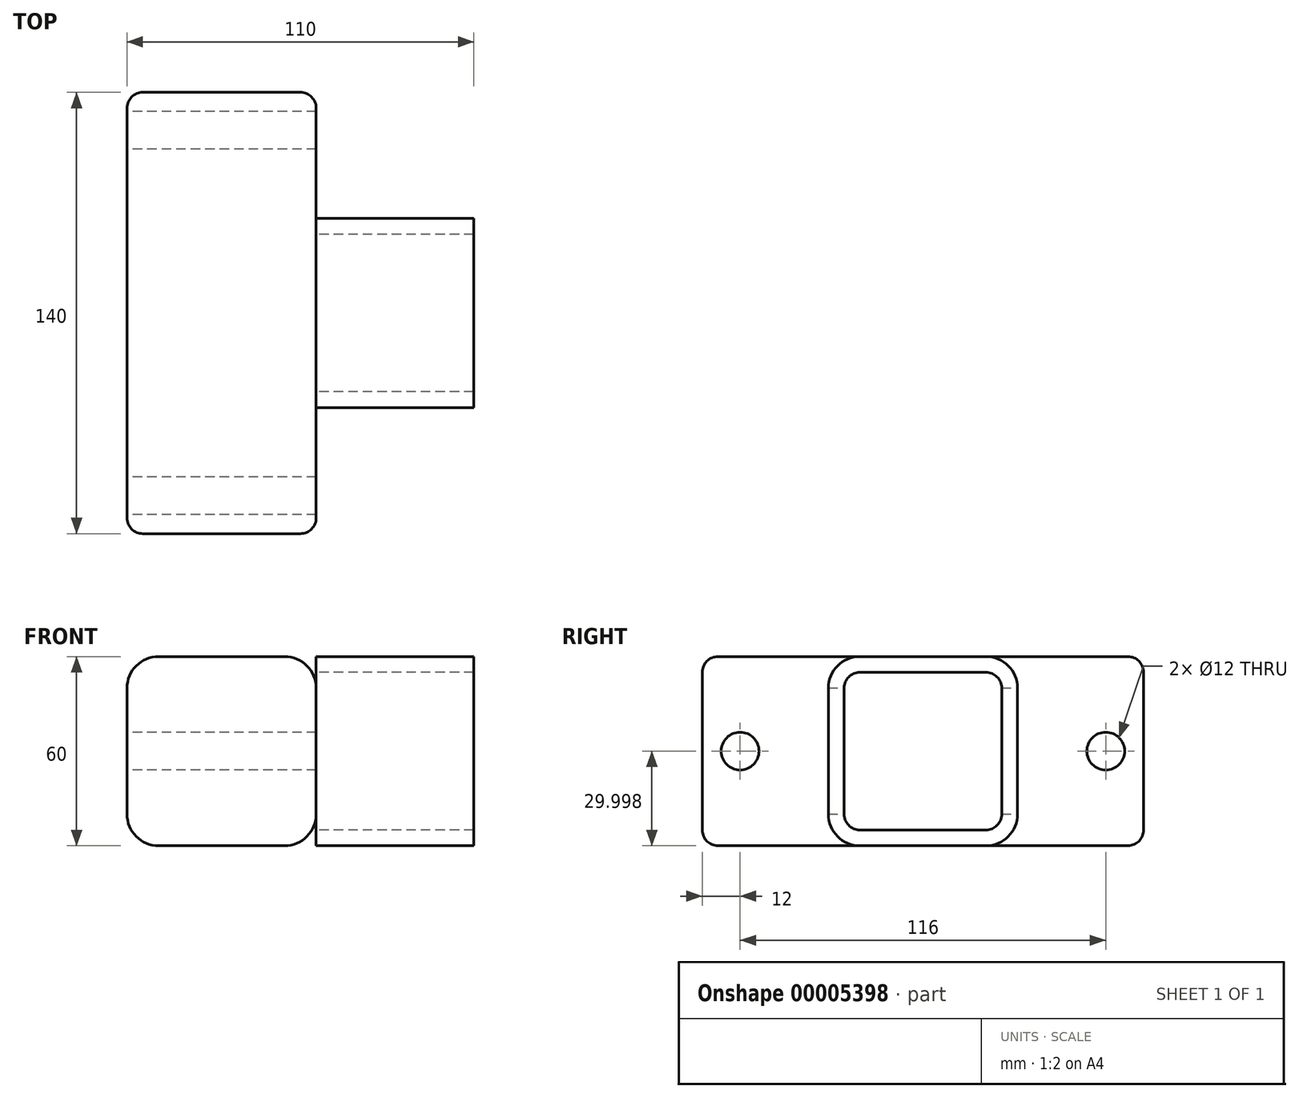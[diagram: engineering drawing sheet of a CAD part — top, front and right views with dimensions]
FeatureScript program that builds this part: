
annotation { "Feature Type Name" : "Feature", "Feature Type Description" : "" }
export const myFeature = defineFeature(function(context is Context, id is Id, definition is map)
    precondition{}
    {
        {
            var Q0;
            Q0=qCreatedBy(makeId("Front.planeOp"),FACE);
            var sketch = newSketch(context, id + "F0", { "sketchPlane" : qUnion([Q0])});
            skLineSegment(sketch, "E0.bottom", {"start": v(-52.29, 66.03) * mm, "end": v(-12.29, 66.03) * mm});
            skLineSegment(sketch, "E0.top", {"start": v(-52.29, 6.03) * mm, "end": v(-12.29, 6.03) * mm});
            skLineSegment(sketch, "E0.left", {"start": v(-62.29, 56.03) * mm, "end": v(-62.29, 16.03) * mm});
            skLineSegment(sketch, "E0.right", {"start": v(-2.29, 56.03) * mm, "end": v(-2.29, 16.03) * mm});
            skLineSegment(sketch, "E1.0", {"start": v(-57.29, 65.96) * mm, "end": v(-57.29, 65.96) * mm});
            skLineSegment(sketch, "E2.0", {"start": v(-52.29, 60.96) * mm, "end": v(-12.29, 60.96) * mm});
            skLineSegment(sketch, "E3.0", {"start": v(-52.29, 11.03) * mm, "end": v(-12.29, 11.03) * mm});
            skLineSegment(sketch, "E3.1", {"start": v(-57.29, 65.96) * mm, "end": v(-57.29, 61.03) * mm});
            skLineSegment(sketch, "E4.0", {"start": v(-7.29, 66.03) * mm, "end": v(-7.29, 65.96) * mm});
            skLineSegment(sketch, "E5.trimOffspring", {"start": v(-7.29, 65.96) * mm, "end": v(2.71, 65.96) * mm});
            skLineSegment(sketch, "E6.trimOffspring", {"start": v(-57.29, 55.96) * mm, "end": v(-57.29, 16.03) * mm});
            skLineSegment(sketch, "E7.trimOffspring", {"start": v(-7.29, 55.96) * mm, "end": v(-7.29, 16.03) * mm});
            skPoint(sketch, "E8.visualSharp", {"position": v(-62.29, 66.03) * mm});
            skArc(sketch, "E8.filletArc", {"start": v(-52.29, 66.03) * mm, "mid": v(-59.36, 63.1) * mm, "end": v(-62.29, 56.03) * mm});
            skPoint(sketch, "E9.visualSharp", {"position": v(-2.29, 66.03) * mm});
            skArc(sketch, "E9.filletArc", {"start": v(-2.29, 56.03) * mm, "mid": v(-5.22, 63.1) * mm, "end": v(-12.29, 66.03) * mm});
            skPoint(sketch, "E10.visualSharp", {"position": v(-2.29, 6.03) * mm});
            skArc(sketch, "E10.filletArc", {"start": v(-12.29, 6.03) * mm, "mid": v(-5.22, 8.96) * mm, "end": v(-2.29, 16.03) * mm});
            skPoint(sketch, "E11.visualSharp", {"position": v(-62.29, 6.03) * mm});
            skArc(sketch, "E11.filletArc", {"start": v(-62.29, 16.03) * mm, "mid": v(-59.36, 8.96) * mm, "end": v(-52.29, 6.03) * mm});
            skPoint(sketch, "E12.visualSharp", {"position": v(-57.29, 60.96) * mm});
            skArc(sketch, "E12.filletArc", {"start": v(-52.29, 60.96) * mm, "mid": v(-55.83, 59.5) * mm, "end": v(-57.29, 55.96) * mm});
            skPoint(sketch, "E13.visualSharp", {"position": v(-7.29, 60.96) * mm});
            skArc(sketch, "E13.filletArc", {"start": v(-7.29, 55.96) * mm, "mid": v(-8.75, 59.5) * mm, "end": v(-12.29, 60.96) * mm});
            skPoint(sketch, "E14.visualSharp", {"position": v(-7.29, 11.03) * mm});
            skArc(sketch, "E14.filletArc", {"start": v(-12.29, 11.03) * mm, "mid": v(-8.75, 12.5) * mm, "end": v(-7.29, 16.03) * mm});
            skPoint(sketch, "E15.visualSharp", {"position": v(-57.29, 11.03) * mm});
            skArc(sketch, "E15.filletArc", {"start": v(-57.29, 16.03) * mm, "mid": v(-55.83, 12.5) * mm, "end": v(-52.29, 11.03) * mm});
            skSolve(sketch);
        }
        {
            var Q0;
            {var subQ4=sQuery(id+"F0.wireOp",EDGE,"E0.bottom");Q0=makeQuery(id+"F0.imprint","IMPRINT",FACE,{"disambiguationData":[TD([[makeQuery(id+"F0.imprint","IMPRINT",EDGE,{"derivedFrom":subQ4}),-1.0]])]});}
            var Q1;
            Q1=makeQuery(id+"F0.imprint","IMPRINT",FACE,{"disambiguationData":[TD([[makeQuery(id+"F0.imprint","IMPRINT",EDGE,{"derivedFrom":sQuery(id+"F0.wireOp",EDGE,"E2.0")}),-1.0]])]});
            extrude(context, id + "F1", {"entities" : qUnion([Q0, Q1]), "depth" : 140 * mm});
        }
        {
            var Q0;
            Q0=makeQuery(id+"F1.opExtrude","SWEPT_FACE",FACE,{"disambiguationData":[OSD([sQuery(id+"F0.wireOp",EDGE,"E0.left")])]});
            var sketch = newSketch(context, id + "F2", { "sketchPlane" : qUnion([Q0])});
            skCircle(sketch, "E16", {"center": v(128, 36.03) * mm, "radius": 6 * mm});
            skCircle(sketch, "E17", {"center": v(12, 36.03) * mm, "radius": 6 * mm});
            skSolve(sketch);
        }
        {
            var Q0;
            Q0=makeQuery(id+"F2.imprint","IMPRINT",FACE,{"disambiguationData":[TD([[makeQuery(id+"F2.imprint","IMPRINT",EDGE,{"derivedFrom":sQuery(id+"F2.wireOp",EDGE,"E17")}),1.0]])]});
            var Q1;
            Q1=makeQuery(id+"F2.imprint","IMPRINT",FACE,{"disambiguationData":[TD([[makeQuery(id+"F2.imprint","IMPRINT",EDGE,{"derivedFrom":sQuery(id+"F2.wireOp",EDGE,"E16")}),1.0]])]});
            extrude(context, id + "F3", {"entities" : qUnion([Q0, Q1]), "operationType" : NewBodyOperationType.REMOVE, "endBound" : BoundingType.THROUGH_ALL, "oppositeDirection" : true, "depth" : 25 * mm});
        }
        {
            var Q0;
            Q0=makeQuery(id+"F1.opExtrude","SWEPT_FACE",FACE,{"disambiguationData":[OSD([sQuery(id+"F0.wireOp",EDGE,"E0.right")])]});
            var sketch = newSketch(context, id + "F4", { "sketchPlane" : qUnion([Q0])});
            skLineSegment(sketch, "E18.bottom", {"start": v(-90, 6.03) * mm, "end": v(-50, 6.03) * mm});
            skLineSegment(sketch, "E18.top", {"start": v(-90, 66.03) * mm, "end": v(-50, 66.03) * mm});
            skLineSegment(sketch, "E18.left", {"start": v(-100, 16.03) * mm, "end": v(-100, 56.03) * mm});
            skLineSegment(sketch, "E18.right", {"start": v(-40, 16.03) * mm, "end": v(-40, 56.03) * mm});
            skLineSegment(sketch, "E19.0", {"start": v(-90, 11.03) * mm, "end": v(-50, 11.03) * mm});
            skLineSegment(sketch, "E20.0", {"start": v(-95, 16.03) * mm, "end": v(-95, 56.03) * mm});
            skLineSegment(sketch, "E21.0", {"start": v(-45, 16.03) * mm, "end": v(-45, 56.03) * mm});
            skLineSegment(sketch, "E22.0", {"start": v(-90, 61.03) * mm, "end": v(-50, 61.03) * mm});
            skPoint(sketch, "E23.visualSharp", {"position": v(-95, 11.03) * mm});
            skArc(sketch, "E23.filletArc", {"start": v(-95, 16.03) * mm, "mid": v(-93.54, 12.5) * mm, "end": v(-90, 11.03) * mm});
            skPoint(sketch, "E24.visualSharp", {"position": v(-45, 11.03) * mm});
            skArc(sketch, "E24.filletArc", {"start": v(-50, 11.03) * mm, "mid": v(-46.46, 12.5) * mm, "end": v(-45, 16.03) * mm});
            skPoint(sketch, "E25.visualSharp", {"position": v(-45, 61.03) * mm});
            skArc(sketch, "E25.filletArc", {"start": v(-45, 56.03) * mm, "mid": v(-46.46, 59.56) * mm, "end": v(-50, 61.03) * mm});
            skPoint(sketch, "E26.visualSharp", {"position": v(-95, 61.03) * mm});
            skArc(sketch, "E26.filletArc", {"start": v(-90, 61.03) * mm, "mid": v(-93.54, 59.56) * mm, "end": v(-95, 56.03) * mm});
            skPoint(sketch, "E27.visualSharp", {"position": v(-100, 6.03) * mm});
            skArc(sketch, "E27.filletArc", {"start": v(-100, 16.03) * mm, "mid": v(-97.07, 8.96) * mm, "end": v(-90, 6.03) * mm});
            skPoint(sketch, "E28.visualSharp", {"position": v(-40, 6.03) * mm});
            skArc(sketch, "E28.filletArc", {"start": v(-50, 6.03) * mm, "mid": v(-42.93, 8.96) * mm, "end": v(-40, 16.03) * mm});
            skPoint(sketch, "E29.visualSharp", {"position": v(-40, 66.03) * mm});
            skArc(sketch, "E29.filletArc", {"start": v(-40, 56.03) * mm, "mid": v(-42.93, 63.1) * mm, "end": v(-50, 66.03) * mm});
            skPoint(sketch, "E30.visualSharp", {"position": v(-100, 66.03) * mm});
            skArc(sketch, "E30.filletArc", {"start": v(-90, 66.03) * mm, "mid": v(-97.07, 63.1) * mm, "end": v(-100, 56.03) * mm});
            skSolve(sketch);
        }
        {
            var Q0;
            Q0=makeQuery(id+"F4.imprint","IMPRINT",FACE,{"disambiguationData":[TD([[makeQuery(id+"F4.imprint","IMPRINT",EDGE,{"derivedFrom":sQuery(id+"F4.wireOp",EDGE,"E18.top")}),-1.0]])]});
            var Q1;
            {var subQ3=sQuery(id+"F4.wireOp",EDGE,"E18.right");Q1=makeQuery(id+"F4.imprint","IMPRINT",FACE,{"disambiguationData":[TD([[makeQuery(id+"F4.imprint","IMPRINT",EDGE,{"derivedFrom":subQ3}),1.0]])]});}
            var Q2;
            Q2=makeQuery(id+"F4.imprint","IMPRINT",FACE,{"disambiguationData":[TD([[makeQuery(id+"F4.imprint","IMPRINT",EDGE,{"derivedFrom":sQuery(id+"F4.wireOp",EDGE,"E18.bottom")}),1.0]])]});
            var Q3;
            {var subQ3=sQuery(id+"F4.wireOp",EDGE,"E18.left");Q3=makeQuery(id+"F4.imprint","IMPRINT",FACE,{"disambiguationData":[TD([[makeQuery(id+"F4.imprint","IMPRINT",EDGE,{"derivedFrom":subQ3}),-1.0]])]});}
            extrude(context, id + "F5", {"entities" : qUnion([Q0, Q1, Q2, Q3]), "operationType" : NewBodyOperationType.ADD, "depth" : 50 * mm});
        }
        {
            var Q0;
            Q0=makeQuery(id+"F1.opExtrude","CAP_EDGE",EDGE,{"disambiguationData":[OSD([sQuery(id+"F0.wireOp",EDGE,"E0.right")])],"isStart":false});
            var Q1;
            Q1=makeQuery(id+"F1.opExtrude","CAP_EDGE",EDGE,{"disambiguationData":[OSD([sQuery(id+"F0.wireOp",EDGE,"E0.top")])],"isStart":true});
            fillet(context, id + "F6", {"entities" : qUnion([Q0, Q1]), "radius" : 5 * mm, "tangentPropagation" : true, "allowEdgeOverflow" : false});
        }
    });
